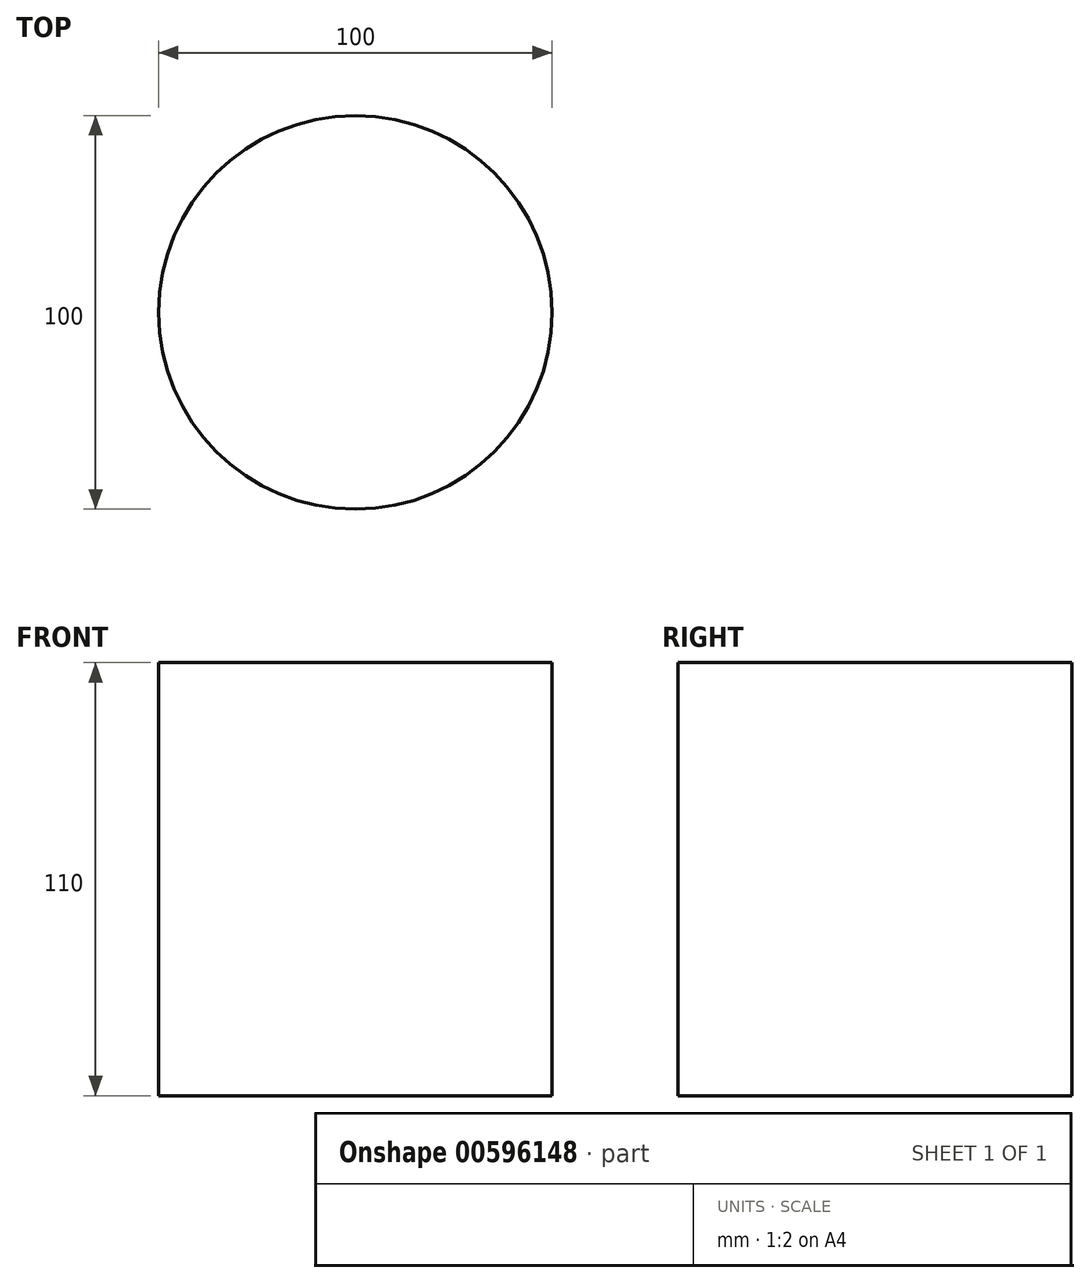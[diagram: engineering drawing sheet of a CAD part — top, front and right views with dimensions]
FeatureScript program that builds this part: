
annotation { "Feature Type Name" : "Feature", "Feature Type Description" : "" }
export const myFeature = defineFeature(function(context is Context, id is Id, definition is map)
    precondition{}
    {
        {
            var Q0;
            Q0=qCreatedBy(makeId("Top.planeOp"),FACE);
            var sketch = newSketch(context, id + "F0", { "sketchPlane" : qUnion([Q0])});
            skCircle(sketch, "E0", {"center": v(0, 0) * mm, "radius": 50 * mm});
            skSolve(sketch);
        }
        {
            var Q0;
            Q0 = qSketchRegion(id + "F0", true);
            extrude(context, id + "F1", {"entities" : qUnion([Q0]), "depth" : 110 * mm, "offsetDistance" : 25 * mm});
        }
    });
